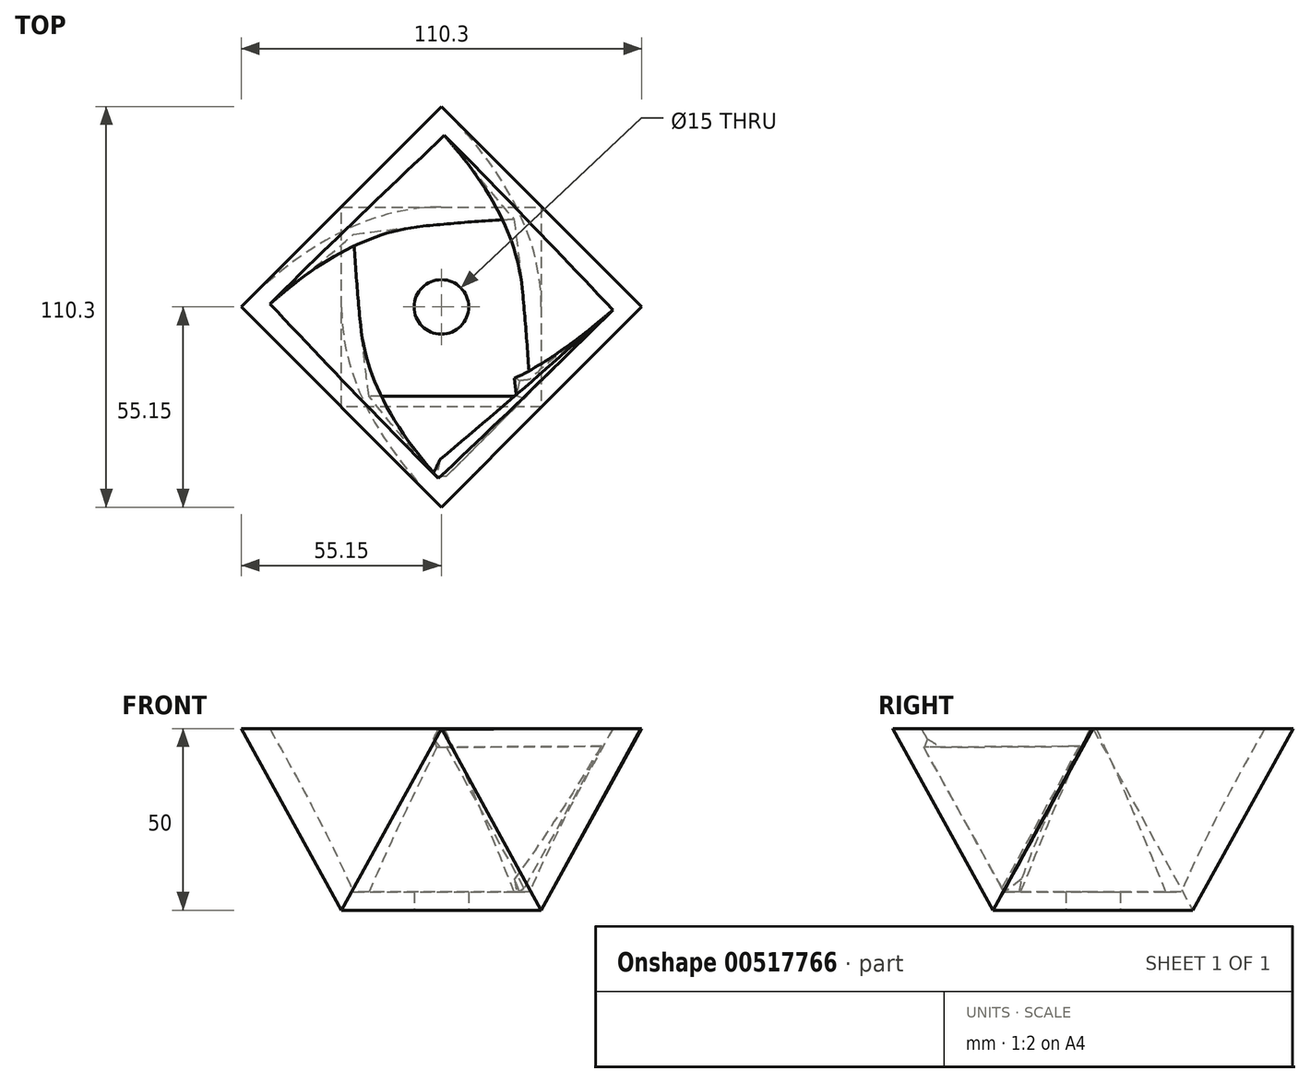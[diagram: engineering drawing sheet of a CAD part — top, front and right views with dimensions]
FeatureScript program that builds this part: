
annotation { "Feature Type Name" : "Feature", "Feature Type Description" : "" }
export const myFeature = defineFeature(function(context is Context, id is Id, definition is map)
    precondition{}
    {
        {
            var Q0;
            Q0=qCreatedBy(makeId("Top.planeOp"),FACE);
            var sketch = newSketch(context, id + "F0", { "sketchPlane" : qUnion([Q0])});
            skCircle(sketch, "E0.cCircle", {"center": v(0, 0) * mm, "radius": 27.5 * mm, "construction": true});
            skLineSegment(sketch, "E0.0", {"start": v(-27.5, 27.5) * mm, "end": v(27.5, 27.5) * mm});
            skLineSegment(sketch, "E0.1", {"start": v(27.5, 27.5) * mm, "end": v(27.5, -27.5) * mm});
            skLineSegment(sketch, "E0.2", {"start": v(27.5, -27.5) * mm, "end": v(-27.5, -27.5) * mm});
            skLineSegment(sketch, "E0.3", {"start": v(-27.5, -27.5) * mm, "end": v(-27.5, 27.5) * mm});
            skPoint(sketch, "E0.0.midPoint", {"position": v(0, 27.5) * mm});
            skSolve(sketch);
        }
        {
            var Q0;
            Q0=qCreatedBy(makeId("Top.planeOp"),FACE);
            cPlane(context, id + "F1", {"entities" : qUnion([Q0]), "cplaneType" : CPlaneType.OFFSET, "offset" : 50 * mm, "width" : 150 * mm, "height" : 150 * mm});
        }
        {
            var Q0;
            Q0=qCreatedBy(id+"F1.planeOp",FACE);
            var sketch = newSketch(context, id + "F2", { "sketchPlane" : qUnion([Q0])});
            skCircle(sketch, "E1.cCircle", {"center": v(0, 0) * mm, "radius": 39 * mm, "construction": true});
            skLineSegment(sketch, "E1.0", {"start": v(0, 55.15) * mm, "end": v(55.15, 0) * mm});
            skLineSegment(sketch, "E1.1", {"start": v(55.15, 0) * mm, "end": v(0, -55.15) * mm});
            skLineSegment(sketch, "E1.2", {"start": v(0, -55.15) * mm, "end": v(-55.15, 0) * mm});
            skLineSegment(sketch, "E1.3", {"start": v(-55.15, 0) * mm, "end": v(0, 55.15) * mm});
            skPoint(sketch, "E1.0.midPoint", {"position": v(27.58, 27.58) * mm});
            skPoint(sketch, "E2.0", {"position": v(27.5, 27.5) * mm});
            skLineSegment(sketch, "E3.0", {"start": v(-27.5, 27.5) * mm, "end": v(27.5, 27.5) * mm, "construction": true});
            skSolve(sketch);
        }
        {
            var Q0;
            Q0=sQuery(id+"F2.wireOp",VERTEX,"E1.2.start");
            var Q1;
            Q1=sQuery(id+"F0.wireOp",VERTEX,"E0.3.start");
            var Q2;
            Q2=sQuery(id+"F0.wireOp",VERTEX,"E0.2.start");
            cPlane(context, id + "F3", {"entities" : qUnion([Q0, Q1, Q2]), "cplaneType" : CPlaneType.THREE_POINT, "offset" : 25 * mm, "width" : 150 * mm, "height" : 150 * mm});
        }
        {
            var Q0;
            Q0=qCreatedBy(id+"F3.planeOp",FACE);
            var sketch = newSketch(context, id + "F4", { "sketchPlane" : qUnion([Q0])});
            skPoint(sketch, "E4.0", {"position": v(0, 70.45) * mm});
            skPoint(sketch, "E5.0", {"position": v(27.5, 13.3) * mm});
            skPoint(sketch, "E6.0", {"position": v(-27.5, 13.3) * mm});
            skLineSegment(sketch, "E7", {"start": v(0, 70.45) * mm, "end": v(-27.5, 13.3) * mm});
            skLineSegment(sketch, "E8", {"start": v(-27.5, 13.3) * mm, "end": v(27.5, 13.3) * mm});
            skLineSegment(sketch, "E9", {"start": v(27.5, 13.3) * mm, "end": v(0, 70.45) * mm});
            skSolve(sketch);
        }
        {
            var Q0;
            Q0=sQuery(id+"F4.wireOp",VERTEX,"E4.0");
            var Q1;
            Q1=sQuery(id+"F4.wireOp",VERTEX,"E6.0");
            var Q2;
            Q2=sQuery(id+"F2.wireOp",VERTEX,"E1.0.end");
            cPlane(context, id + "F5", {"entities" : qUnion([Q0, Q1, Q2]), "cplaneType" : CPlaneType.THREE_POINT, "offset" : 25 * mm, "width" : 150 * mm, "height" : 150 * mm});
        }
        {
            var Q0;
            Q0=qCreatedBy(id+"F5.planeOp",FACE);
            var sketch = newSketch(context, id + "F6", { "sketchPlane" : qUnion([Q0])});
            skPoint(sketch, "E10.0", {"position": v(39.1, 50) * mm});
            skPoint(sketch, "E11.0", {"position": v(0, 0.08) * mm});
            skPoint(sketch, "E12.0", {"position": v(-38.9, 50.17) * mm});
            skLineSegment(sketch, "E13", {"start": v(-38.9, 50.17) * mm, "end": v(39.1, 50) * mm});
            skLineSegment(sketch, "E14", {"start": v(39.1, 50) * mm, "end": v(0, 0.08) * mm});
            skLineSegment(sketch, "E15", {"start": v(-38.9, 50.17) * mm, "end": v(0, 0.08) * mm});
            skSolve(sketch);
        }
        {
            var Q0;
            Q0=makeQuery(id+"F2.imprint","IMPRINT",FACE,{"disambiguationData":[TD([[makeQuery(id+"F2.imprint","IMPRINT",EDGE,{"derivedFrom":sQuery(id+"F2.wireOp",EDGE,"E1.0")}),-1.0]])]});
            var Q1;
            Q1=makeQuery(id+"F0.imprint","IMPRINT",FACE,{"disambiguationData":[TD([[makeQuery(id+"F0.imprint","IMPRINT",EDGE,{"derivedFrom":sQuery(id+"F0.wireOp",EDGE,"E0.0")}),-1.0]])]});
            loft(context, id + "F7", {"sheetProfilesArray" : [{ "sheetProfileEntities" : qUnion([Q0]) }, { "sheetProfileEntities" : qUnion([Q1]) }]});
        }
        {
            var Q0;
            Q0 = qSketchRegion(id + "F4", true);
            var Q1;
            Q1=makeQuery(id+"F7.opLoft","SWEPT_BODY",BODY,{"disambiguationData":[OSD([makeQuery(id+"F0.imprint","IMPRINT",FACE,{"disambiguationData":[TD([[makeQuery(id+"F0.imprint","IMPRINT",EDGE,{"derivedFrom":sQuery(id+"F0.wireOp",EDGE,"E0.0")}),-1.0]])]}),makeQuery(id+"F2.imprint","IMPRINT",FACE,{"disambiguationData":[TD([[makeQuery(id+"F2.imprint","IMPRINT",EDGE,{"derivedFrom":sQuery(id+"F2.wireOp",EDGE,"E1.0")}),-1.0]])]})])]});
            extrude(context, id + "F8", {"entities" : qUnion([Q0]), "operationType" : NewBodyOperationType.ADD, "endBound" : BoundingType.UP_TO_BODY, "depth" : 25 * mm, "endBoundEntityBody" : qUnion([Q1]), "offsetDistance" : 25 * mm});
        }
        {
            var Q0;
            Q0 = qSketchRegion(id + "F6", true);
            var Q1;
            Q1=makeQuery(id+"F7.opLoft","SWEPT_BODY",BODY,{"disambiguationData":[OSD([makeQuery(id+"F0.imprint","IMPRINT",FACE,{"disambiguationData":[TD([[makeQuery(id+"F0.imprint","IMPRINT",EDGE,{"derivedFrom":sQuery(id+"F0.wireOp",EDGE,"E0.0")}),-1.0]])]}),makeQuery(id+"F2.imprint","IMPRINT",FACE,{"disambiguationData":[TD([[makeQuery(id+"F2.imprint","IMPRINT",EDGE,{"derivedFrom":sQuery(id+"F2.wireOp",EDGE,"E1.0")}),-1.0]])]})])]});
            extrude(context, id + "F9", {"entities" : qUnion([Q0]), "operationType" : NewBodyOperationType.ADD, "endBound" : BoundingType.UP_TO_BODY, "depth" : 25 * mm, "endBoundEntityBody" : qUnion([Q1]), "offsetDistance" : 25 * mm});
        }
        {
            var Q0;
            Q0=makeQuery(id+"F7.opLoft","CAP_FACE",FACE,{"disambiguationData":[OSD([makeQuery(id+"F2.imprint","IMPRINT",FACE,{"disambiguationData":[TD([[makeQuery(id+"F2.imprint","IMPRINT",EDGE,{"derivedFrom":sQuery(id+"F2.wireOp",EDGE,"E1.0")}),-1.0]])]})])],"isStart":true});
            shell(context, id + "F10", {"entities" : qUnion([Q0]), "thickness" : 5 * mm});
        }
        {
            var Q0;
            Q0=sQuery(id+"F0.wireOp",VERTEX,"E0.cCircle.center");
            var Q1;
            Q1=makeQuery(id+"F7.opLoft","SWEPT_BODY",BODY,{"disambiguationData":[OSD([makeQuery(id+"F0.imprint","IMPRINT",FACE,{"disambiguationData":[TD([[makeQuery(id+"F0.imprint","IMPRINT",EDGE,{"derivedFrom":sQuery(id+"F0.wireOp",EDGE,"E0.0")}),-1.0]])]}),makeQuery(id+"F2.imprint","IMPRINT",FACE,{"disambiguationData":[TD([[makeQuery(id+"F2.imprint","IMPRINT",EDGE,{"derivedFrom":sQuery(id+"F2.wireOp",EDGE,"E1.0")}),-1.0]])]})])]});
            hole(context, id + "F11", {"style" : HoleStyle.SIMPLE, "endStyle" : HoleEndStyle.THROUGH, "oppositeDirection" : true, "holeDiameter" : 15 * mm, "isTappedThrough" : true, "tappedDepth" : 12 * mm, "tapClearance" : 3, "startFromSketch" : true, "locations" : qUnion([Q0]), "scope" : qUnion([Q1])});
        }
    });
